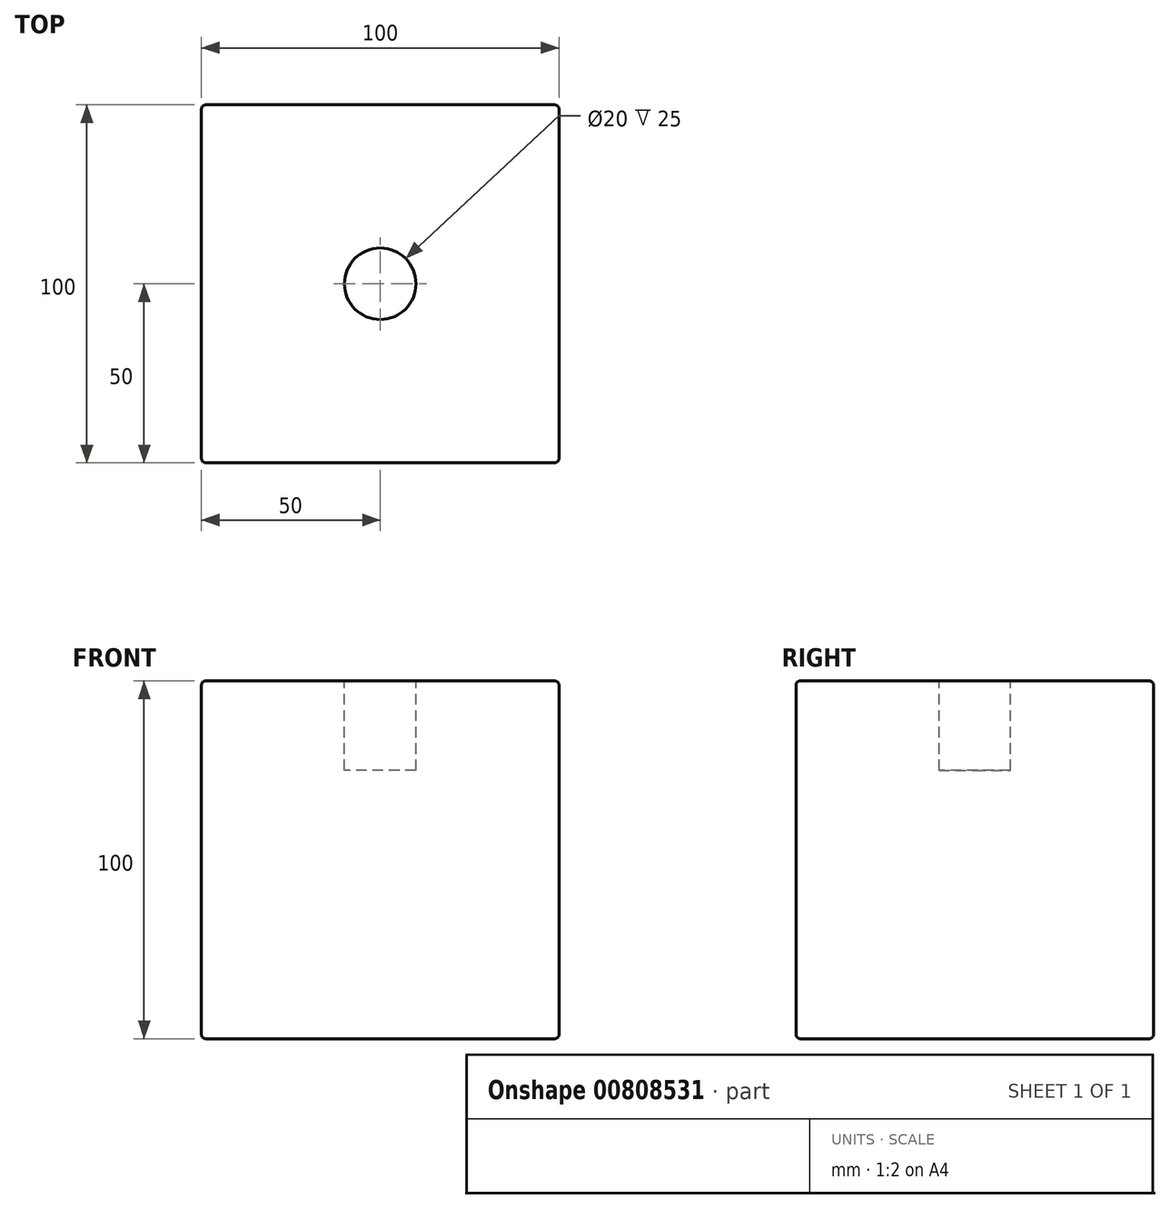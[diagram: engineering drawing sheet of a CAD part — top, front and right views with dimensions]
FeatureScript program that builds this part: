
annotation { "Feature Type Name" : "Feature", "Feature Type Description" : "" }
export const myFeature = defineFeature(function(context is Context, id is Id, definition is map)
    precondition{}
    {
        {
            var Q0;
            Q0=qCreatedBy(makeId("Top.planeOp"),FACE);
            var sketch = newSketch(context, id + "F0", { "sketchPlane" : qUnion([Q0])});
            skLineSegment(sketch, "E0.bottom", {"start": v(50, -50) * mm, "end": v(-50, -50) * mm});
            skLineSegment(sketch, "E0.top", {"start": v(50, 50) * mm, "end": v(-50, 50) * mm});
            skLineSegment(sketch, "E0.left", {"start": v(50, -50) * mm, "end": v(50, 50) * mm});
            skLineSegment(sketch, "E0.right", {"start": v(-50, -50) * mm, "end": v(-50, 50) * mm});
            skPoint(sketch, "E0.middle", {"position": v(0, 0) * mm});
            skSolve(sketch);
        }
        {
            var Q0;
            Q0 = qSketchRegion(id + "F0", true);
            extrude(context, id + "F1", {"entities" : qUnion([Q0]), "depth" : 100 * mm, "offsetDistance" : 25 * mm});
        }
        {
            var Q0;
            Q0=makeQuery(id+"F1.opExtrude","CAP_FACE",FACE,{"disambiguationData":[OSD([sQuery(id+"F0.wireOp",EDGE,"E0.bottom"),sQuery(id+"F0.wireOp",EDGE,"E0.top"),sQuery(id+"F0.wireOp",EDGE,"E0.left"),sQuery(id+"F0.wireOp",EDGE,"E0.right")])],"isStart":false});
            var sketch = newSketch(context, id + "F2", { "sketchPlane" : qUnion([Q0])});
            skCircle(sketch, "E1", {"center": v(0, 0) * mm, "radius": 10 * mm});
            skSolve(sketch);
        }
        {
            var Q0;
            Q0=makeQuery(id+"F2.imprint","IMPRINT",FACE,{"disambiguationData":[TD([[makeQuery(id+"F2.imprint","IMPRINT",EDGE,{"derivedFrom":sQuery(id+"F2.wireOp",EDGE,"E1")}),1.0]])]});
            extrude(context, id + "F3", {"entities" : qUnion([Q0]), "operationType" : NewBodyOperationType.REMOVE, "oppositeDirection" : true, "depth" : 25 * mm, "offsetDistance" : 25 * mm});
        }
        {
            var Q0;
            Q0=makeQuery(id+"F1.opExtrude","CAP_EDGE",EDGE,{"disambiguationData":[OSD([sQuery(id+"F0.wireOp",EDGE,"E0.right")])],"isStart":false});
            var Q1;
            Q1=makeQuery(id+"F1.opExtrude","CAP_EDGE",EDGE,{"disambiguationData":[OSD([sQuery(id+"F0.wireOp",EDGE,"E0.top")])],"isStart":false});
            var Q2;
            Q2=makeQuery(id+"F1.opExtrude","CAP_EDGE",EDGE,{"disambiguationData":[OSD([sQuery(id+"F0.wireOp",EDGE,"E0.left")])],"isStart":false});
            var Q3;
            Q3=makeQuery(id+"F1.opExtrude","CAP_EDGE",EDGE,{"disambiguationData":[OSD([sQuery(id+"F0.wireOp",EDGE,"E0.bottom")])],"isStart":false});
            var Q4;
            Q4=makeQuery(id+"F1.opExtrude","SWEPT_EDGE",EDGE,{"disambiguationData":[OSD([sQuery(id+"F0.wireOp",EDGE,"E0.bottom"),sQuery(id+"F0.wireOp",EDGE,"E0.right")])]});
            var Q5;
            Q5=makeQuery(id+"F1.opExtrude","SWEPT_EDGE",EDGE,{"disambiguationData":[OSD([sQuery(id+"F0.wireOp",EDGE,"E0.top"),sQuery(id+"F0.wireOp",EDGE,"E0.right")])]});
            var Q6;
            Q6=makeQuery(id+"F1.opExtrude","SWEPT_EDGE",EDGE,{"disambiguationData":[OSD([sQuery(id+"F0.wireOp",EDGE,"E0.bottom"),sQuery(id+"F0.wireOp",EDGE,"E0.left")])]});
            var Q7;
            Q7=makeQuery(id+"F1.opExtrude","SWEPT_EDGE",EDGE,{"disambiguationData":[OSD([sQuery(id+"F0.wireOp",EDGE,"E0.top"),sQuery(id+"F0.wireOp",EDGE,"E0.left")])]});
            var Q8;
            Q8=makeQuery(id+"F1.opExtrude","CAP_EDGE",EDGE,{"disambiguationData":[OSD([sQuery(id+"F0.wireOp",EDGE,"E0.left")])],"isStart":true});
            var Q9;
            Q9=makeQuery(id+"F1.opExtrude","CAP_EDGE",EDGE,{"disambiguationData":[OSD([sQuery(id+"F0.wireOp",EDGE,"E0.bottom")])],"isStart":true});
            var Q10;
            Q10=makeQuery(id+"F1.opExtrude","CAP_EDGE",EDGE,{"disambiguationData":[OSD([sQuery(id+"F0.wireOp",EDGE,"E0.right")])],"isStart":true});
            var Q11;
            Q11=makeQuery(id+"F1.opExtrude","CAP_EDGE",EDGE,{"disambiguationData":[OSD([sQuery(id+"F0.wireOp",EDGE,"E0.top")])],"isStart":true});
            fillet(context, id + "F4", {"entities" : qUnion([Q0, Q1, Q2, Q3, Q4, Q5, Q6, Q7, Q8, Q9, Q10, Q11]), "radius" : 1.2 * mm, "tangentPropagation" : true, "allowEdgeOverflow" : false});
        }
    });
